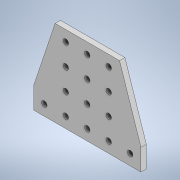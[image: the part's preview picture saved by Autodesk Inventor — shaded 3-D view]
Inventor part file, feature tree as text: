
AUTODESK INVENTOR PART (.ipt)
format: ipt  version: 2020 (Build 240168000, 168)  size: 131,584 bytes
history: native  units: in
note: dims shown in document units (in); Inventor stores cm internally (conversion verified against a paired STEP export)
features: extrude x1, sketch x1
ambient origin geometry x8: Origin, YZ Plane, XZ Plane, XY Plane, X Axis, Y Axis, Z Axis, Center Point
bodies: Solid1 (feature_tree)
feature tree (2):
  extrude  "Extrusion1"  Depth=4.0in
  sketch  "Sketch1"  dims[d2=5.0in d3=4.0in d4=0.256in d5=0.5in d6=0.5in d7=1.9685in d9=1.0in d10=0.3937in d12=1.0in d14=1.0in d15=1.0in d16=1.5748in d18=1.0in d19=0.3937in d21=1.0in d23=1.0in d24=1.0in d25=0.25in d26=0.0in]
